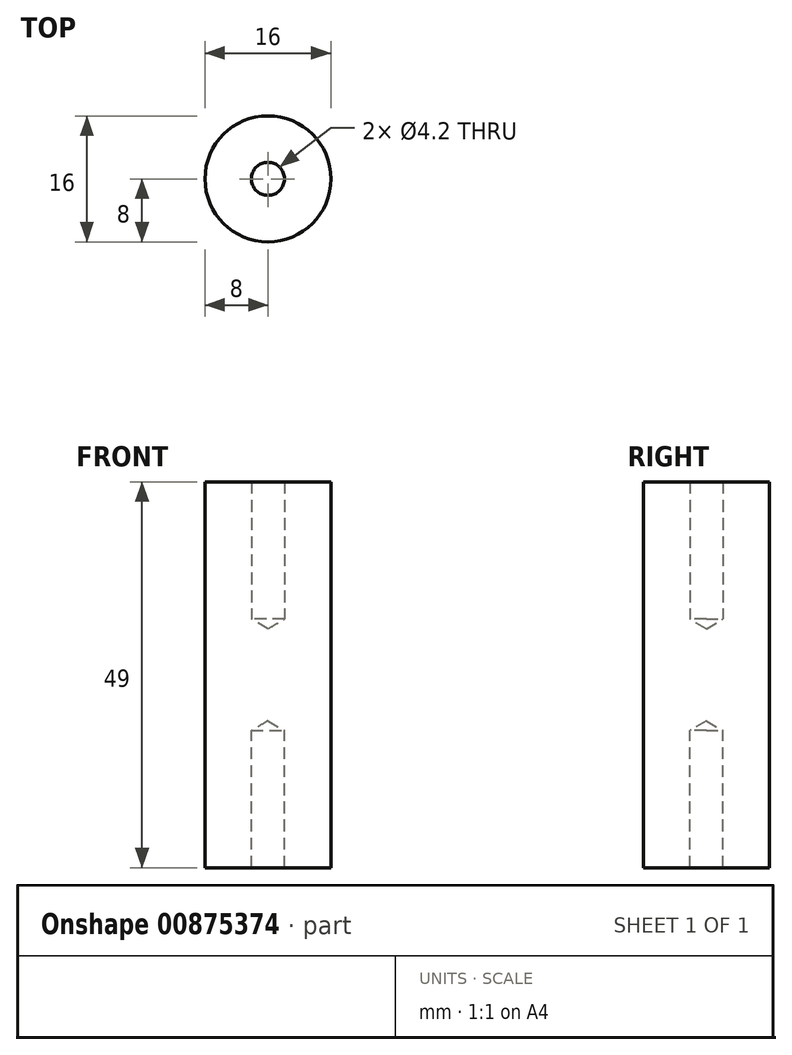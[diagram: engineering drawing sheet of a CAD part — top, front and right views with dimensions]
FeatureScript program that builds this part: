
annotation { "Feature Type Name" : "Feature", "Feature Type Description" : "" }
export const myFeature = defineFeature(function(context is Context, id is Id, definition is map)
    precondition{}
    {
        {
            var Q0;
            Q0=qCreatedBy(makeId("Top.planeOp"),FACE);
            var sketch = newSketch(context, id + "F0", { "sketchPlane" : qUnion([Q0])});
            skCircle(sketch, "E0", {"center": v(0, 0) * mm, "radius": 8 * mm});
            skSolve(sketch);
        }
        {
            var Q0;
            Q0=makeQuery(id+"F0.imprint","IMPRINT",FACE,{"disambiguationData":[TD([[makeQuery(id+"F0.imprint","IMPRINT",EDGE,{"derivedFrom":sQuery(id+"F0.wireOp",EDGE,"E0")}),1.0]])]});
            extrude(context, id + "F1", {"entities" : qUnion([Q0]), "depth" : 49 * mm, "offsetDistance" : 25 * mm});
        }
        {
            var Q0;
            Q0=makeQuery(id+"F1.opExtrude","CAP_FACE",FACE,{"disambiguationData":[OSD([sQuery(id+"F0.wireOp",EDGE,"E0")])],"isStart":false});
            var sketch = newSketch(context, id + "F2", { "sketchPlane" : qUnion([Q0])});
            skPoint(sketch, "E1", {"position": v(0, 0) * mm});
            skSolve(sketch);
        }
        {
            var Q0;
            Q0=sQuery(id+"F2.wireOp",VERTEX,"E1");
            var Q1;
            Q1=makeQuery(id+"F1.opExtrude","SWEPT_BODY",BODY,{"disambiguationData":[OSD([sQuery(id+"F0.wireOp",EDGE,"E0")])]});
            hole(context, id + "F3", {"style" : HoleStyle.SIMPLE, "endStyle" : HoleEndStyle.BLIND, "standardTappedOrClearance" : lookupTablePath({ "standard" : "ISO", "engagement" : "75%", "pitch" : "0.8 mm", "size" : "M5", "type" : "Tapped" }), "standardBlindInLast" : lookupTablePath({ "standard" : "ISO", "engagement" : "75%", "pitch" : "0.8 mm", "size" : "M5", "type" : "Tapped" }), "holeDiameter" : 4.2 * mm, "majorDiameter" : 5 * mm, "showTappedDepth" : true, "holeDepth" : 17.4 * mm, "isTappedThrough" : true, "tappedDepth" : 15 * mm, "tapClearance" : 3, "locations" : qUnion([Q0]), "scope" : qUnion([Q1]), "startStyle" : HoleStartStyle.SKETCH});
        }
        {
            var Q0;
            Q0=makeQuery(id+"F1.opExtrude","CAP_FACE",FACE,{"disambiguationData":[OSD([sQuery(id+"F0.wireOp",EDGE,"E0")])],"isStart":true});
            var sketch = newSketch(context, id + "F4", { "sketchPlane" : qUnion([Q0])});
            skPoint(sketch, "E2", {"position": v(0, 0) * mm});
            skSolve(sketch);
        }
        {
            var Q0;
            Q0=sQuery(id+"F4.wireOp",VERTEX,"E2");
            var Q1;
            Q1=makeQuery(id+"F1.opExtrude","SWEPT_BODY",BODY,{"disambiguationData":[OSD([sQuery(id+"F0.wireOp",EDGE,"E0")])]});
            hole(context, id + "F5", {"style" : HoleStyle.SIMPLE, "endStyle" : HoleEndStyle.BLIND, "standardTappedOrClearance" : lookupTablePath({ "standard" : "ISO", "engagement" : "75%", "pitch" : "0.8 mm", "size" : "M5", "type" : "Tapped" }), "standardBlindInLast" : lookupTablePath({ "standard" : "ISO", "engagement" : "75%", "pitch" : "0.8 mm", "size" : "M5", "type" : "Tapped" }), "holeDiameter" : 4.2 * mm, "majorDiameter" : 5 * mm, "showTappedDepth" : true, "holeDepth" : 17.4 * mm, "isTappedThrough" : true, "tappedDepth" : 15 * mm, "tapClearance" : 3, "locations" : qUnion([Q0]), "scope" : qUnion([Q1]), "startStyle" : HoleStartStyle.SKETCH});
        }
    });
